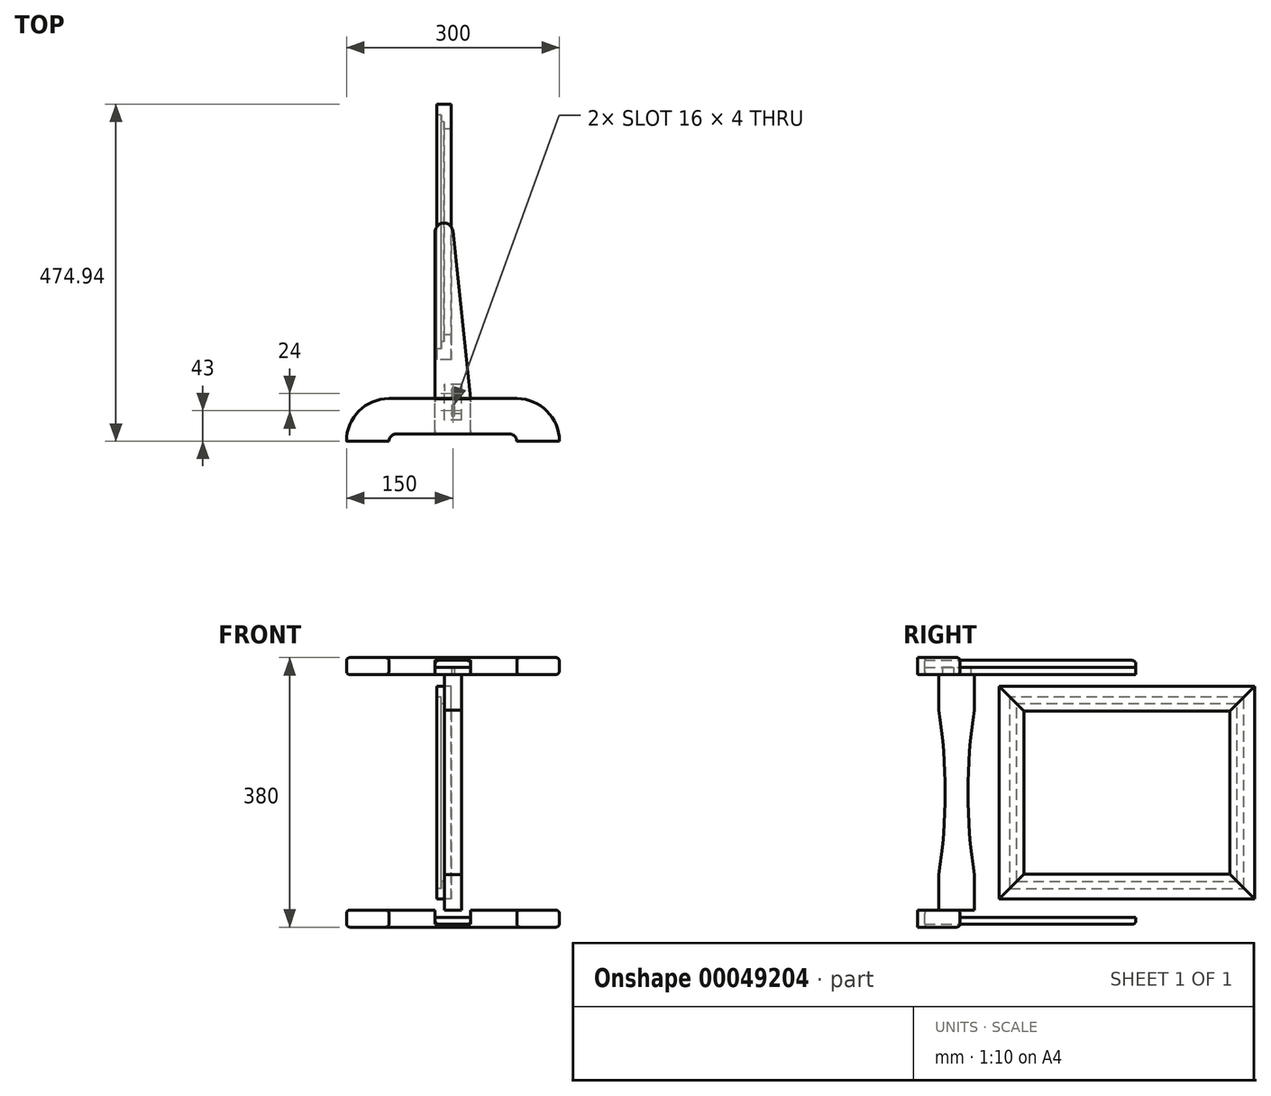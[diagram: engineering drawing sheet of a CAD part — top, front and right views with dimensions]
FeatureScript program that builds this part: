
annotation { "Feature Type Name" : "Feature", "Feature Type Description" : "" }
export const myFeature = defineFeature(function(context is Context, id is Id, definition is map)
    precondition{}
    {
        {
            var Q0;
            Q0=qCreatedBy(makeId("Top.planeOp"),FACE);
            var sketch = newSketch(context, id + "F0", { "sketchPlane" : qUnion([Q0])});
            skLineSegment(sketch, "E0.bottom", {"start": v(150, -30) * mm, "end": v(90, -30) * mm});
            skLineSegment(sketch, "E0.top", {"start": v(90, 30) * mm, "end": v(-90, 30) * mm});
            skPoint(sketch, "E0.middle", {"position": v(0, 0) * mm});
            skArc(sketch, "E1", {"start": v(90, -30) * mm, "mid": v(87.07, -22.93) * mm, "end": v(80, -20) * mm});
            skArc(sketch, "E2", {"start": v(-80, -20) * mm, "mid": v(-87.07, -22.93) * mm, "end": v(-90, -30) * mm});
            skLineSegment(sketch, "E3", {"start": v(-80, -20) * mm, "end": v(80, -20) * mm});
            skArc(sketch, "E4", {"start": v(150, -30) * mm, "mid": v(132.43, 12.43) * mm, "end": v(90, 30) * mm});
            skPoint(sketch, "E0.right.end.orphan", {"position": v(-150, 30) * mm});
            skArc(sketch, "E5.trimOffspring", {"start": v(-90, 30) * mm, "mid": v(-132.43, 12.43) * mm, "end": v(-150, -30) * mm});
            skPoint(sketch, "E0.left.end.orphan", {"position": v(150, 30) * mm});
            skLineSegment(sketch, "E6.trimOffspring", {"start": v(-90, -30) * mm, "end": v(-150, -30) * mm});
            skSolve(sketch);
        }
        {
            var Q0;
            Q0=makeQuery(id+"F0.imprint","IMPRINT",FACE,{"disambiguationData":[TD([[makeQuery(id+"F0.imprint","IMPRINT",EDGE,{"derivedFrom":sQuery(id+"F0.wireOp",EDGE,"E0.bottom")}),-1.0]])]});
            extrude(context, id + "F1", {"entities" : qUnion([Q0]), "depth" : 24 * mm, "offsetDistance" : 25 * mm});
        }
        {
            var Q0;
            Q0=makeQuery(id+"F1.opExtrude","SWEPT_FACE",FACE,{"disambiguationData":[OSD([sQuery(id+"F0.wireOp",EDGE,"E0.top")])]});
            var sketch = newSketch(context, id + "F2", { "sketchPlane" : qUnion([Q0])});
            skLineSegment(sketch, "E7.top", {"start": v(-25, 10) * mm, "end": v(25, 10) * mm});
            skPoint(sketch, "E7.middle", {"position": v(0, 0) * mm});
            skLineSegment(sketch, "E8", {"start": v(25, 0) * mm, "end": v(25, 10) * mm});
            skLineSegment(sketch, "E9", {"start": v(-25, 0) * mm, "end": v(-25, 10) * mm});
            skLineSegment(sketch, "E10", {"start": v(25, 0) * mm, "end": v(-25, 0) * mm});
            skSolve(sketch);
        }
        {
            var Q0;
            Q0=makeQuery(id+"F2.imprint","IMPRINT",FACE,{"disambiguationData":[TD([[makeQuery(id+"F2.imprint","IMPRINT",EDGE,{"derivedFrom":sQuery(id+"F2.wireOp",EDGE,"E7.top")}),-1.0]])]});
            extrude(context, id + "F3", {"entities" : qUnion([Q0]), "operationType" : NewBodyOperationType.REMOVE, "endBound" : BoundingType.THROUGH_ALL, "oppositeDirection" : true, "depth" : 25 * mm, "offsetDistance" : 25 * mm});
        }
        {
            var Q0;
            Q0=makeQuery(id+"F1.opExtrude","CAP_EDGE",EDGE,{"disambiguationData":[OSD([sQuery(id+"F0.wireOp",EDGE,"E5.trimOffspring")])],"isStart":false});
            var Q1;
            Q1=makeQuery(id+"F1.opExtrude","CAP_EDGE",EDGE,{"disambiguationData":[OSD([sQuery(id+"F0.wireOp",EDGE,"E2")])],"isStart":false});
            var Q2;
            Q2=makeQuery(id+"F1.opExtrude","CAP_EDGE",EDGE,{"disambiguationData":[OSD([sQuery(id+"F0.wireOp",EDGE,"E5.trimOffspring")])],"isStart":true});
            var Q3;
            {var subQ0=sQuery(id+"F0.wireOp",EDGE,"E4");var subQ1=sQuery(id+"F0.wireOp",EDGE,"E0.top");Q3=makeQuery(id+"F3.boolean.opBoolean","SPLIT",EDGE,{"disambiguationData":[TD([makeQuery(id+"F1.opExtrude","SWEPT_FACE",FACE,{"disambiguationData":[OSD([subQ0])]})])],"derivedFrom":makeQuery(id+"F1.opExtrude","CAP_EDGE",EDGE,{"disambiguationData":[OSD([subQ1])],"isStart":true})});}
            var Q4;
            Q4=makeQuery(id+"F1.opExtrude","CAP_EDGE",EDGE,{"disambiguationData":[OSD([sQuery(id+"F0.wireOp",EDGE,"E1")])],"isStart":true});
            var Q5;
            {var subQ0=sQuery(id+"F0.wireOp",EDGE,"E3");var subQ1=sQuery(id+"F0.wireOp",EDGE,"E2");Q5=makeQuery(id+"F3.boolean.opBoolean","SPLIT",EDGE,{"disambiguationData":[TD([makeQuery(id+"F1.opExtrude","SWEPT_FACE",FACE,{"disambiguationData":[OSD([subQ1])]})])],"derivedFrom":makeQuery(id+"F1.opExtrude","CAP_EDGE",EDGE,{"disambiguationData":[OSD([subQ0])],"isStart":true})});}
            fillet(context, id + "F4", {"entities" : qUnion([Q0, Q1, Q2, Q3, Q4, Q5]), "radius" : 5 * mm, "tangentPropagation" : true, "allowEdgeOverflow" : false});
        }
        {
            var Q0;
            Q0=qCreatedBy(makeId("Right.planeOp"),FACE);
            var sketch = newSketch(context, id + "F5", { "sketchPlane" : qUnion([Q0])});
            skLineSegment(sketch, "E11", {"start": v(-20.06, 0) * mm, "end": v(29.94, 0) * mm});
            skLineSegment(sketch, "E12", {"start": v(29.94, 0) * mm, "end": v(29.94, -50) * mm});
            skLineSegment(sketch, "E13", {"start": v(29.94, -332) * mm, "end": v(-20.06, -332) * mm});
            skLineSegment(sketch, "E14", {"start": v(-20.06, -332) * mm, "end": v(-20.06, -282) * mm});
            skLineSegment(sketch, "E15", {"start": v(46, -50) * mm, "end": v(-37.65, -50) * mm, "construction": true});
            skLineSegment(sketch, "E16", {"start": v(48.69, -282) * mm, "end": v(-41.5, -282) * mm, "construction": true});
            skArc(sketch, "E17", {"start": v(29.94, -50) * mm, "mid": v(20.92, -166) * mm, "end": v(29.94, -282) * mm});
            skPoint(sketch, "E17.first.point", {"position": v(29.94, -50) * mm});
            skPoint(sketch, "E17.second.point", {"position": v(29.94, -282) * mm});
            skArc(sketch, "E18", {"start": v(-20.06, -282) * mm, "mid": v(-11.03, -166) * mm, "end": v(-20.06, -50) * mm});
            skPoint(sketch, "E18.first.point", {"position": v(-20.06, -50) * mm});
            skPoint(sketch, "E18.second.point", {"position": v(-20.06, -282) * mm});
            skLineSegment(sketch, "E19.trimOffspring", {"start": v(29.94, -282) * mm, "end": v(29.94, -332) * mm});
            skLineSegment(sketch, "E20.trimOffspring", {"start": v(-20.06, -50) * mm, "end": v(-20.06, 0) * mm});
            skSolve(sketch);
        }
        {
            var Q0;
            Q0=makeQuery(id+"F5.imprint","IMPRINT",FACE,{"disambiguationData":[TD([[makeQuery(id+"F5.imprint","IMPRINT",EDGE,{"derivedFrom":sQuery(id+"F5.wireOp",EDGE,"E11")}),-1.0]])]});
            extrude(context, id + "F6", {"entities" : qUnion([Q0]), "depth" : 24 * mm, "offsetDistance" : 25 * mm, "symmetric" : true});
        }
        {
            var Q0;
            Q0=qCreatedBy(makeId("Right.planeOp"),FACE);
            var sketch = newSketch(context, id + "F7", { "sketchPlane" : qUnion([Q0])});
            skLineSegment(sketch, "E21", {"start": v(-60.62, -166) * mm, "end": v(450.96, -166) * mm, "construction": true});
            skLineSegment(sketch, "E22", {"start": v(264.94, 66.23) * mm, "end": v(264.94, -411.72) * mm, "construction": true});
            skLineSegment(sketch, "E23.bottom", {"start": v(84.94, -316) * mm, "end": v(444.94, -316) * mm});
            skLineSegment(sketch, "E23.top", {"start": v(84.94, -16) * mm, "end": v(444.94, -16) * mm});
            skLineSegment(sketch, "E23.left", {"start": v(84.94, -316) * mm, "end": v(84.94, -16) * mm});
            skLineSegment(sketch, "E23.right", {"start": v(444.94, -316) * mm, "end": v(444.94, -16) * mm});
            skPoint(sketch, "E23.middle", {"position": v(264.94, -166) * mm});
            skSolve(sketch);
        }
        {
            var Q0;
            Q0=makeQuery(id+"F6.opExtrude","SWEPT_BODY",BODY,{"disambiguationData":[OSD([sQuery(id+"F5.wireOp",EDGE,"E11"),sQuery(id+"F5.wireOp",EDGE,"E12"),sQuery(id+"F5.wireOp",EDGE,"E13"),sQuery(id+"F5.wireOp",EDGE,"E14"),sQuery(id+"F5.wireOp",EDGE,"E17"),sQuery(id+"F5.wireOp",EDGE,"E18"),sQuery(id+"F5.wireOp",EDGE,"E19.trimOffspring"),sQuery(id+"F5.wireOp",EDGE,"E20.trimOffspring")])]});
            transform(context, id + "F8", {"entities" : qUnion([Q0]), "transformType" : TransformType.TRANSLATION_3D, "dx" : 0 * mm, "dy" : -100 * mm, "dz" : 0 * mm, "makeCopy" : false});
        }
        {
            var Q0;
            Q0=makeQuery(id+"F6.opExtrude","SWEPT_BODY",BODY,{"disambiguationData":[OSD([sQuery(id+"F5.wireOp",EDGE,"E11"),sQuery(id+"F5.wireOp",EDGE,"E12"),sQuery(id+"F5.wireOp",EDGE,"E13"),sQuery(id+"F5.wireOp",EDGE,"E14"),sQuery(id+"F5.wireOp",EDGE,"E17"),sQuery(id+"F5.wireOp",EDGE,"E18"),sQuery(id+"F5.wireOp",EDGE,"E19.trimOffspring"),sQuery(id+"F5.wireOp",EDGE,"E20.trimOffspring")])]});
            transform(context, id + "F9", {"entities" : qUnion([Q0]), "transformType" : TransformType.TRANSLATION_3D, "dx" : 0 * mm, "dy" : 120 * mm, "dz" : 0 * mm, "makeCopy" : false});
        }
        {
            var Q0;
            Q0=makeQuery(id+"F7.imprint","IMPRINT",FACE,{"disambiguationData":[TD([[makeQuery(id+"F7.imprint","IMPRINT",EDGE,{"derivedFrom":sQuery(id+"F7.wireOp",EDGE,"E23.bottom")}),1.0]])]});
            var sketch = newSketch(context, id + "F10", { "sketchPlane" : qUnion([Q0])});
            skLineSegment(sketch, "E24", {"start": v(409.94, -51) * mm, "end": v(409.94, -281) * mm});
            skLineSegment(sketch, "E25", {"start": v(119.94, -51) * mm, "end": v(119.94, -281) * mm});
            skLineSegment(sketch, "E26", {"start": v(409.94, -281) * mm, "end": v(119.94, -281) * mm});
            skLineSegment(sketch, "E27", {"start": v(409.94, -51) * mm, "end": v(119.94, -51) * mm});
            skPoint(sketch, "E28.orphan", {"position": v(69.8, -281) * mm});
            skPoint(sketch, "E29.orphan", {"position": v(69.8, -51) * mm});
            skLineSegment(sketch, "E30", {"start": v(444.94, -16) * mm, "end": v(409.94, -51) * mm});
            skLineSegment(sketch, "E31", {"start": v(119.94, -281) * mm, "end": v(84.94, -316) * mm});
            skLineSegment(sketch, "E32", {"start": v(409.94, -281) * mm, "end": v(444.94, -316) * mm});
            skLineSegment(sketch, "E33", {"start": v(119.94, -51) * mm, "end": v(84.94, -16) * mm});
            skSolve(sketch);
        }
        {
            var Q0;
            Q0=makeQuery(id+"F10.imprint","IMPRINT",FACE,{"disambiguationData":[TD([[makeQuery(id+"F10.imprint","IMPRINT",EDGE,{"derivedFrom":sQuery(id+"F10.wireOp",EDGE,"E24")}),1.0]])]});
            extrude(context, id + "F11", {"entities" : qUnion([Q0]), "depth" : 10 * mm, "offsetDistance" : 25 * mm});
        }
        {
            var Q0;
            Q0=makeQuery(id+"F11.opExtrude","CAP_FACE",FACE,{"disambiguationData":[OSD([sQuery(id+"F7.wireOp",EDGE,"E23.right"),sQuery(id+"F10.wireOp",EDGE,"E24"),sQuery(id+"F10.wireOp",EDGE,"E30"),sQuery(id+"F10.wireOp",EDGE,"E32")])],"isStart":true});
            extrude(context, id + "F12", {"entities" : qUnion([Q0]), "operationType" : NewBodyOperationType.ADD, "depth" : 10 * mm, "offsetDistance" : 25 * mm});
        }
        {
            var Q0;
            Q0=makeQuery(id+"F10.imprint","IMPRINT",FACE,{"disambiguationData":[TD([[makeQuery(id+"F10.imprint","IMPRINT",EDGE,{"derivedFrom":sQuery(id+"F10.wireOp",EDGE,"E25")}),-1.0]])]});
            extrude(context, id + "F13", {"entities" : qUnion([Q0]), "depth" : 10 * mm, "offsetDistance" : 25 * mm});
        }
        {
            var Q0;
            Q0=makeQuery(id+"F13.opExtrude","CAP_FACE",FACE,{"disambiguationData":[OSD([sQuery(id+"F7.wireOp",EDGE,"E23.left"),sQuery(id+"F10.wireOp",EDGE,"E25"),sQuery(id+"F10.wireOp",EDGE,"E31"),sQuery(id+"F10.wireOp",EDGE,"E33")])],"isStart":true});
            extrude(context, id + "F14", {"entities" : qUnion([Q0]), "operationType" : NewBodyOperationType.ADD, "depth" : 10 * mm, "offsetDistance" : 25 * mm});
        }
        {
            var Q0;
            Q0=makeQuery(id+"F10.imprint","IMPRINT",FACE,{"disambiguationData":[TD([[makeQuery(id+"F10.imprint","IMPRINT",EDGE,{"derivedFrom":sQuery(id+"F10.wireOp",EDGE,"E27")}),-1.0]])]});
            extrude(context, id + "F15", {"entities" : qUnion([Q0]), "depth" : 10 * mm, "offsetDistance" : 25 * mm});
        }
        {
            var Q0;
            Q0=makeQuery(id+"F15.opExtrude","CAP_FACE",FACE,{"disambiguationData":[OSD([sQuery(id+"F7.wireOp",EDGE,"E23.top"),sQuery(id+"F10.wireOp",EDGE,"E27"),sQuery(id+"F10.wireOp",EDGE,"E30"),sQuery(id+"F10.wireOp",EDGE,"E33")])],"isStart":true});
            extrude(context, id + "F16", {"entities" : qUnion([Q0]), "depth" : 10 * mm, "offsetDistance" : 25 * mm});
        }
        {
            var Q0;
            Q0=makeQuery(id+"F10.imprint","IMPRINT",FACE,{"disambiguationData":[TD([[makeQuery(id+"F10.imprint","IMPRINT",EDGE,{"derivedFrom":sQuery(id+"F10.wireOp",EDGE,"E26")}),1.0]])]});
            extrude(context, id + "F17", {"entities" : qUnion([Q0]), "depth" : 10 * mm, "offsetDistance" : 25 * mm});
        }
        {
            var Q0;
            Q0=makeQuery(id+"F17.opExtrude","CAP_FACE",FACE,{"disambiguationData":[OSD([sQuery(id+"F7.wireOp",EDGE,"E23.bottom"),sQuery(id+"F10.wireOp",EDGE,"E26"),sQuery(id+"F10.wireOp",EDGE,"E31"),sQuery(id+"F10.wireOp",EDGE,"E32")])],"isStart":true});
            extrude(context, id + "F18", {"entities" : qUnion([Q0]), "depth" : 10 * mm, "offsetDistance" : 25 * mm});
        }
        {
            var Q0;
            Q0=makeQuery(id+"F16.opExtrude","SWEPT_BODY",BODY,{"disambiguationData":[OSD([sQuery(id+"F7.wireOp",EDGE,"E23.top"),sQuery(id+"F10.wireOp",EDGE,"E27"),sQuery(id+"F10.wireOp",EDGE,"E30"),sQuery(id+"F10.wireOp",EDGE,"E33")])]});
            var Q1;
            Q1=makeQuery(id+"F15.opExtrude","SWEPT_BODY",BODY,{"disambiguationData":[OSD([sQuery(id+"F7.wireOp",EDGE,"E23.top"),sQuery(id+"F10.wireOp",EDGE,"E27"),sQuery(id+"F10.wireOp",EDGE,"E30"),sQuery(id+"F10.wireOp",EDGE,"E33")])]});
            booleanBodies(context, id + "F19", {"operationType" : BooleanOperationType.UNION, "tools" : qUnion([Q0, Q1])});
        }
        {
            var Q0;
            Q0=makeQuery(id+"F17.opExtrude","SWEPT_BODY",BODY,{"disambiguationData":[OSD([sQuery(id+"F7.wireOp",EDGE,"E23.bottom"),sQuery(id+"F10.wireOp",EDGE,"E26"),sQuery(id+"F10.wireOp",EDGE,"E31"),sQuery(id+"F10.wireOp",EDGE,"E32")])]});
            var Q1;
            Q1=makeQuery(id+"F18.opExtrude","SWEPT_BODY",BODY,{"disambiguationData":[OSD([sQuery(id+"F7.wireOp",EDGE,"E23.bottom"),sQuery(id+"F10.wireOp",EDGE,"E26"),sQuery(id+"F10.wireOp",EDGE,"E31"),sQuery(id+"F10.wireOp",EDGE,"E32")])]});
            booleanBodies(context, id + "F20", {"operationType" : BooleanOperationType.UNION, "tools" : qUnion([Q0, Q1])});
        }
        {
            var Q0;
            Q0=makeQuery(id+"F12.opExtrude","CAP_FACE",FACE,{"disambiguationData":[OSD([sQuery(id+"F7.wireOp",EDGE,"E23.right"),sQuery(id+"F10.wireOp",EDGE,"E24"),sQuery(id+"F10.wireOp",EDGE,"E30"),sQuery(id+"F10.wireOp",EDGE,"E32")])],"isStart":false});
            var sketch = newSketch(context, id + "F21", { "sketchPlane" : qUnion([Q0])});
            skLineSegment(sketch, "E34", {"start": v(-419.94, -291) * mm, "end": v(-419.94, -41) * mm});
            skSolve(sketch);
        }
        {
            var Q0;
            {var subQ0=sQuery(id+"F21.wireOp",EDGE,"E34");Q0=makeQuery(id+"F21.imprint","IMPRINT",FACE,{"disambiguationData":[TD([[makeQuery(id+"F21.imprint","IMPRINT",EDGE,{"derivedFrom":subQ0}),-1.0]])]});}
            extrude(context, id + "F22", {"entities" : qUnion([Q0]), "operationType" : NewBodyOperationType.REMOVE, "oppositeDirection" : true, "depth" : 10 * mm, "offsetDistance" : 25 * mm});
        }
        {
            var Q0;
            Q0=makeQuery(id+"F12.opExtrude","CAP_FACE",FACE,{"disambiguationData":[OSD([sQuery(id+"F7.wireOp",EDGE,"E23.right"),sQuery(id+"F10.wireOp",EDGE,"E24"),sQuery(id+"F10.wireOp",EDGE,"E30"),sQuery(id+"F10.wireOp",EDGE,"E32")])],"isStart":false});
            var sketch = newSketch(context, id + "F23", { "sketchPlane" : qUnion([Q0])});
            skLineSegment(sketch, "E35", {"start": v(-429.94, -301) * mm, "end": v(-429.94, -31) * mm});
            skSolve(sketch);
        }
        {
            var Q0;
            Q0 = qSketchRegion(id + "F23", true);
            var Q1;
            {var subQ0=sQuery(id+"F23.wireOp",EDGE,"E35");Q1=makeQuery(id+"F23.imprint","IMPRINT",FACE,{"disambiguationData":[TD([[makeQuery(id+"F23.imprint","IMPRINT",EDGE,{"derivedFrom":subQ0}),-1.0]])]});}
            extrude(context, id + "F24", {"entities" : qUnion([Q0, Q1]), "operationType" : NewBodyOperationType.REMOVE, "oppositeDirection" : true, "depth" : 6 * mm, "offsetDistance" : 25 * mm});
        }
        {
            var Q0;
            Q0=makeQuery(id+"F16.opExtrude","CAP_FACE",FACE,{"disambiguationData":[OSD([sQuery(id+"F7.wireOp",EDGE,"E23.top"),sQuery(id+"F10.wireOp",EDGE,"E27"),sQuery(id+"F10.wireOp",EDGE,"E30"),sQuery(id+"F10.wireOp",EDGE,"E33")])],"isStart":false});
            var sketch = newSketch(context, id + "F25", { "sketchPlane" : qUnion([Q0])});
            skLineSegment(sketch, "E36", {"start": v(-419.94, -41) * mm, "end": v(-109.94, -41) * mm});
            skSolve(sketch);
        }
        {
            var Q0;
            Q0 = qSketchRegion(id + "F25", true);
            var Q1;
            {var subQ0=sQuery(id+"F25.wireOp",EDGE,"E36");Q1=makeQuery(id+"F25.imprint","IMPRINT",FACE,{"disambiguationData":[TD([[makeQuery(id+"F25.imprint","IMPRINT",EDGE,{"derivedFrom":subQ0}),-1.0]])]});}
            extrude(context, id + "F26", {"entities" : qUnion([Q0, Q1]), "operationType" : NewBodyOperationType.REMOVE, "oppositeDirection" : true, "depth" : 10 * mm, "offsetDistance" : 25 * mm});
        }
        {
            var Q0;
            Q0=makeQuery(id+"F16.opExtrude","CAP_FACE",FACE,{"disambiguationData":[OSD([sQuery(id+"F7.wireOp",EDGE,"E23.top"),sQuery(id+"F10.wireOp",EDGE,"E27"),sQuery(id+"F10.wireOp",EDGE,"E30"),sQuery(id+"F10.wireOp",EDGE,"E33")])],"isStart":false});
            var sketch = newSketch(context, id + "F27", { "sketchPlane" : qUnion([Q0])});
            skLineSegment(sketch, "E37", {"start": v(-429.94, -31) * mm, "end": v(-99.94, -31) * mm});
            skSolve(sketch);
        }
        {
            var Q0;
            Q0 = qSketchRegion(id + "F27", true);
            var Q1;
            {var subQ0=sQuery(id+"F27.wireOp",EDGE,"E37");Q1=makeQuery(id+"F27.imprint","IMPRINT",FACE,{"disambiguationData":[TD([[makeQuery(id+"F27.imprint","IMPRINT",EDGE,{"derivedFrom":subQ0}),-1.0]])]});}
            extrude(context, id + "F28", {"entities" : qUnion([Q0, Q1]), "operationType" : NewBodyOperationType.REMOVE, "oppositeDirection" : true, "depth" : 6 * mm, "offsetDistance" : 25 * mm});
        }
        {
            var Q0;
            Q0=makeQuery(id+"F18.opExtrude","CAP_FACE",FACE,{"disambiguationData":[OSD([sQuery(id+"F7.wireOp",EDGE,"E23.bottom"),sQuery(id+"F10.wireOp",EDGE,"E26"),sQuery(id+"F10.wireOp",EDGE,"E31"),sQuery(id+"F10.wireOp",EDGE,"E32")])],"isStart":false});
            var sketch = newSketch(context, id + "F29", { "sketchPlane" : qUnion([Q0])});
            skLineSegment(sketch, "E38", {"start": v(-109.94, -291) * mm, "end": v(-419.94, -291) * mm});
            skSolve(sketch);
        }
        {
            var Q0;
            Q0 = qSketchRegion(id + "F29", true);
            var Q1;
            {var subQ0=sQuery(id+"F29.wireOp",EDGE,"E38");Q1=makeQuery(id+"F29.imprint","IMPRINT",FACE,{"disambiguationData":[TD([[makeQuery(id+"F29.imprint","IMPRINT",EDGE,{"derivedFrom":subQ0}),-1.0]])]});}
            extrude(context, id + "F30", {"entities" : qUnion([Q0, Q1]), "operationType" : NewBodyOperationType.REMOVE, "oppositeDirection" : true, "depth" : 10 * mm, "offsetDistance" : 25 * mm});
        }
        {
            var Q0;
            Q0=makeQuery(id+"F18.opExtrude","CAP_FACE",FACE,{"disambiguationData":[OSD([sQuery(id+"F7.wireOp",EDGE,"E23.bottom"),sQuery(id+"F10.wireOp",EDGE,"E26"),sQuery(id+"F10.wireOp",EDGE,"E31"),sQuery(id+"F10.wireOp",EDGE,"E32")])],"isStart":false});
            var sketch = newSketch(context, id + "F31", { "sketchPlane" : qUnion([Q0])});
            skLineSegment(sketch, "E39", {"start": v(-99.94, -301) * mm, "end": v(-429.94, -301) * mm});
            skSolve(sketch);
        }
        {
            var Q0;
            Q0 = qSketchRegion(id + "F31", true);
            var Q1;
            {var subQ0=sQuery(id+"F31.wireOp",EDGE,"E39");Q1=makeQuery(id+"F31.imprint","IMPRINT",FACE,{"disambiguationData":[TD([[makeQuery(id+"F31.imprint","IMPRINT",EDGE,{"derivedFrom":subQ0}),-1.0]])]});}
            extrude(context, id + "F32", {"entities" : qUnion([Q0, Q1]), "operationType" : NewBodyOperationType.REMOVE, "oppositeDirection" : true, "depth" : 6 * mm, "offsetDistance" : 25 * mm});
        }
        {
            var Q0;
            Q0=makeQuery(id+"F14.opExtrude","CAP_FACE",FACE,{"disambiguationData":[OSD([sQuery(id+"F7.wireOp",EDGE,"E23.left"),sQuery(id+"F10.wireOp",EDGE,"E25"),sQuery(id+"F10.wireOp",EDGE,"E31"),sQuery(id+"F10.wireOp",EDGE,"E33")])],"isStart":false});
            var sketch = newSketch(context, id + "F33", { "sketchPlane" : qUnion([Q0])});
            skLineSegment(sketch, "E40", {"start": v(-109.94, -291) * mm, "end": v(-109.94, -41) * mm});
            skSolve(sketch);
        }
        {
            var Q0;
            Q0 = qSketchRegion(id + "F33", true);
            var Q1;
            {var subQ0=sQuery(id+"F33.wireOp",EDGE,"E40");Q1=makeQuery(id+"F33.imprint","IMPRINT",FACE,{"disambiguationData":[TD([[makeQuery(id+"F33.imprint","IMPRINT",EDGE,{"derivedFrom":subQ0}),1.0]])]});}
            extrude(context, id + "F34", {"entities" : qUnion([Q0, Q1]), "operationType" : NewBodyOperationType.REMOVE, "oppositeDirection" : true, "depth" : 10 * mm, "offsetDistance" : 25 * mm});
        }
        {
            var Q0;
            Q0=makeQuery(id+"F14.opExtrude","CAP_FACE",FACE,{"disambiguationData":[OSD([sQuery(id+"F7.wireOp",EDGE,"E23.left"),sQuery(id+"F10.wireOp",EDGE,"E25"),sQuery(id+"F10.wireOp",EDGE,"E31"),sQuery(id+"F10.wireOp",EDGE,"E33")])],"isStart":false});
            var sketch = newSketch(context, id + "F35", { "sketchPlane" : qUnion([Q0])});
            skLineSegment(sketch, "E41", {"start": v(-99.94, -301) * mm, "end": v(-99.94, -31) * mm});
            skSolve(sketch);
        }
        {
            var Q0;
            Q0 = qSketchRegion(id + "F35", true);
            var Q1;
            {var subQ0=sQuery(id+"F35.wireOp",EDGE,"E41");Q1=makeQuery(id+"F35.imprint","IMPRINT",FACE,{"disambiguationData":[TD([[makeQuery(id+"F35.imprint","IMPRINT",EDGE,{"derivedFrom":subQ0}),1.0]])]});}
            extrude(context, id + "F36", {"entities" : qUnion([Q0, Q1]), "operationType" : NewBodyOperationType.REMOVE, "oppositeDirection" : true, "depth" : 6 * mm, "offsetDistance" : 25 * mm});
        }
        {
            var Q0;
            Q0=makeQuery(id+"F3.boolean.opBoolean","COPY",FACE,{"derivedFrom":makeQuery(id+"F3.opExtrude","SWEPT_FACE",FACE,{"disambiguationData":[OSD([sQuery(id+"F2.wireOp",EDGE,"E7.top")])]})});
            var sketch = newSketch(context, id + "F37", { "sketchPlane" : qUnion([Q0])});
            skLineSegment(sketch, "E42", {"start": v(25, -30) * mm, "end": v(25, 20) * mm});
            skLineSegment(sketch, "E43", {"start": v(25, 20) * mm, "end": v(-25, 20) * mm});
            skLineSegment(sketch, "E44", {"start": v(-25, 20) * mm, "end": v(-25, -367.5) * mm});
            skLineSegment(sketch, "E45", {"start": v(118.88, -265) * mm, "end": v(-159.6, -265) * mm, "construction": true});
            skLineSegment(sketch, "E46", {"start": v(-12.5, -305.3) * mm, "end": v(-12.5, 20) * mm, "construction": true});
            skArc(sketch, "E47", {"start": v(-25, -265) * mm, "mid": v(-12.5, -277.5) * mm, "end": v(0, -265) * mm});
            skLineSegment(sketch, "E48", {"start": v(25, -30) * mm, "end": v(-0.07, -266.32) * mm});
            skSolve(sketch);
        }
        {
            var Q0;
            Q0=makeQuery(id+"F37.imprint","IMPRINT",FACE,{"disambiguationData":[TD([[makeQuery(id+"F37.imprint","IMPRINT",EDGE,{"derivedFrom":sQuery(id+"F37.wireOp",EDGE,"E42")}),-1.0]])]});
            var Q1;
            {var subQ4=sQuery(id+"F37.wireOp",EDGE,"E48");Q1=makeQuery(id+"F37.imprint","IMPRINT",FACE,{"disambiguationData":[TD([[makeQuery(id+"F37.imprint","IMPRINT",EDGE,{"derivedFrom":subQ4}),-1.0]])]});}
            extrude(context, id + "F38", {"entities" : qUnion([Q0, Q1]), "depth" : 10 * mm, "offsetDistance" : 25 * mm});
        }
        {
            var Q0;
            Q0=makeQuery(id+"F38.opExtrude","CAP_FACE",FACE,{"disambiguationData":[OSD([sQuery(id+"F37.wireOp",EDGE,"E42"),sQuery(id+"F37.wireOp",EDGE,"E43"),sQuery(id+"F37.wireOp",EDGE,"E44"),sQuery(id+"F37.wireOp",EDGE,"E47"),sQuery(id+"F37.wireOp",EDGE,"E48")])],"isStart":true});
            extrude(context, id + "F39", {"entities" : qUnion([Q0]), "depth" : 10 * mm, "offsetDistance" : 25 * mm});
        }
        {
            var Q0;
            Q0=makeQuery(id+"F39.opExtrude","CAP_FACE",FACE,{"disambiguationData":[OSD([sQuery(id+"F37.wireOp",EDGE,"E42"),sQuery(id+"F37.wireOp",EDGE,"E43"),sQuery(id+"F37.wireOp",EDGE,"E44"),sQuery(id+"F37.wireOp",EDGE,"E47"),sQuery(id+"F37.wireOp",EDGE,"E48")])],"isStart":false});
            var sketch = newSketch(context, id + "F40", { "sketchPlane" : qUnion([Q0])});
            skLineSegment(sketch, "E49", {"start": v(25, 30) * mm, "end": v(-25, 30) * mm});
            skSolve(sketch);
        }
        {
            var Q0;
            Q0 = qSketchRegion(id + "F40", true);
            var Q1;
            {var subQ0=sQuery(id+"F40.wireOp",EDGE,"E49");Q1=makeQuery(id+"F40.imprint","IMPRINT",FACE,{"disambiguationData":[TD([[makeQuery(id+"F40.imprint","IMPRINT",EDGE,{"derivedFrom":subQ0}),1.0]])]});}
            extrude(context, id + "F41", {"entities" : qUnion([Q0, Q1]), "operationType" : NewBodyOperationType.REMOVE, "oppositeDirection" : true, "depth" : 10 * mm, "offsetDistance" : 25 * mm});
        }
        {
            var Q0;
            Q0=makeQuery(id+"F39.opExtrude","CAP_EDGE",EDGE,{"disambiguationData":[OSD([sQuery(id+"F37.wireOp",EDGE,"E48")])],"isStart":false});
            fillet(context, id + "F42", {"entities" : qUnion([Q0]), "tangentPropagation" : true, "radius" : 5 * mm, "defaultsChanged" : false, "vertexSettings" : [], "allowEdgeOverflow" : false});
        }
        {
            var Q0;
            Q0=makeQuery(id+"F1.opExtrude","SWEPT_BODY",BODY,{"disambiguationData":[OSD([sQuery(id+"F0.wireOp",EDGE,"E0.bottom"),sQuery(id+"F0.wireOp",EDGE,"E0.top"),sQuery(id+"F0.wireOp",EDGE,"E1"),sQuery(id+"F0.wireOp",EDGE,"E2"),sQuery(id+"F0.wireOp",EDGE,"E3"),sQuery(id+"F0.wireOp",EDGE,"E4"),sQuery(id+"F0.wireOp",EDGE,"E5.trimOffspring"),sQuery(id+"F0.wireOp",EDGE,"E6.trimOffspring")])]});
            var Q1;
            Q1=makeQuery(id+"F39.opExtrude","SWEPT_BODY",BODY,{"disambiguationData":[OSD([sQuery(id+"F37.wireOp",EDGE,"E42"),sQuery(id+"F37.wireOp",EDGE,"E43"),sQuery(id+"F37.wireOp",EDGE,"E44"),sQuery(id+"F37.wireOp",EDGE,"E47"),sQuery(id+"F37.wireOp",EDGE,"E48")])]});
            var Q2;
            Q2=makeQuery(id+"F38.opExtrude","CAP_FACE",FACE,{"disambiguationData":[OSD([sQuery(id+"F37.wireOp",EDGE,"E42"),sQuery(id+"F37.wireOp",EDGE,"E43"),sQuery(id+"F37.wireOp",EDGE,"E44"),sQuery(id+"F37.wireOp",EDGE,"E47"),sQuery(id+"F37.wireOp",EDGE,"E48")])],"isStart":false});
            mirror(context, id + "F43", {"entities" : qUnion([Q0, Q1]), "mirrorPlane" : qUnion([Q2])});
        }
        {
            var Q0;
            Q0=makeQuery(id+"F43.opPattern","COPY",BODY,{"derivedFrom":makeQuery(id+"F1.opExtrude","SWEPT_BODY",BODY,{"disambiguationData":[OSD([sQuery(id+"F0.wireOp",EDGE,"E0.bottom"),sQuery(id+"F0.wireOp",EDGE,"E0.top"),sQuery(id+"F0.wireOp",EDGE,"E1"),sQuery(id+"F0.wireOp",EDGE,"E2"),sQuery(id+"F0.wireOp",EDGE,"E3"),sQuery(id+"F0.wireOp",EDGE,"E4"),sQuery(id+"F0.wireOp",EDGE,"E5.trimOffspring"),sQuery(id+"F0.wireOp",EDGE,"E6.trimOffspring")])]}),"instanceName":"1"});
            var Q1;
            Q1=makeQuery(id+"F43.opPattern","COPY",BODY,{"derivedFrom":makeQuery(id+"F39.opExtrude","SWEPT_BODY",BODY,{"disambiguationData":[OSD([sQuery(id+"F37.wireOp",EDGE,"E42"),sQuery(id+"F37.wireOp",EDGE,"E43"),sQuery(id+"F37.wireOp",EDGE,"E44"),sQuery(id+"F37.wireOp",EDGE,"E47"),sQuery(id+"F37.wireOp",EDGE,"E48")])]}),"instanceName":"1"});
            transform(context, id + "F44", {"entities" : qUnion([Q0, Q1]), "transformType" : TransformType.TRANSLATION_3D, "dx" : 0 * mm, "dy" : 0 * mm, "dz" : -332 * mm, "makeCopy" : false});
        }
        {
            var Q0;
            Q0=makeQuery(id+"F11.opExtrude","SWEPT_BODY",BODY,{"disambiguationData":[OSD([sQuery(id+"F7.wireOp",EDGE,"E23.right"),sQuery(id+"F10.wireOp",EDGE,"E24"),sQuery(id+"F10.wireOp",EDGE,"E30"),sQuery(id+"F10.wireOp",EDGE,"E32")])]});
            var Q1;
            Q1=makeQuery(id+"F17.opExtrude","SWEPT_BODY",BODY,{"disambiguationData":[OSD([sQuery(id+"F7.wireOp",EDGE,"E23.bottom"),sQuery(id+"F10.wireOp",EDGE,"E26"),sQuery(id+"F10.wireOp",EDGE,"E31"),sQuery(id+"F10.wireOp",EDGE,"E32")])]});
            var Q2;
            Q2=makeQuery(id+"F16.opExtrude","SWEPT_BODY",BODY,{"disambiguationData":[OSD([sQuery(id+"F7.wireOp",EDGE,"E23.top"),sQuery(id+"F10.wireOp",EDGE,"E27"),sQuery(id+"F10.wireOp",EDGE,"E30"),sQuery(id+"F10.wireOp",EDGE,"E33")])]});
            var Q3;
            Q3=makeQuery(id+"F13.opExtrude","SWEPT_BODY",BODY,{"disambiguationData":[OSD([sQuery(id+"F7.wireOp",EDGE,"E23.left"),sQuery(id+"F10.wireOp",EDGE,"E25"),sQuery(id+"F10.wireOp",EDGE,"E31"),sQuery(id+"F10.wireOp",EDGE,"E33")])]});
            transform(context, id + "F45", {"entities" : qUnion([Q0, Q1, Q2, Q3]), "transformType" : TransformType.TRANSLATION_3D, "dx" : 0 * mm, "dy" : 0 * mm, "dz" : -0.5 * mm, "makeCopy" : false});
        }
        {
            var Q0;
            Q0=makeQuery(id+"F11.opExtrude","SWEPT_BODY",BODY,{"disambiguationData":[OSD([sQuery(id+"F7.wireOp",EDGE,"E23.right"),sQuery(id+"F10.wireOp",EDGE,"E24"),sQuery(id+"F10.wireOp",EDGE,"E30"),sQuery(id+"F10.wireOp",EDGE,"E32")])]});
            var Q1;
            Q1=makeQuery(id+"F17.opExtrude","SWEPT_BODY",BODY,{"disambiguationData":[OSD([sQuery(id+"F7.wireOp",EDGE,"E23.bottom"),sQuery(id+"F10.wireOp",EDGE,"E26"),sQuery(id+"F10.wireOp",EDGE,"E31"),sQuery(id+"F10.wireOp",EDGE,"E32")])]});
            var Q2;
            Q2=makeQuery(id+"F16.opExtrude","SWEPT_BODY",BODY,{"disambiguationData":[OSD([sQuery(id+"F7.wireOp",EDGE,"E23.top"),sQuery(id+"F10.wireOp",EDGE,"E27"),sQuery(id+"F10.wireOp",EDGE,"E30"),sQuery(id+"F10.wireOp",EDGE,"E33")])]});
            var Q3;
            Q3=makeQuery(id+"F13.opExtrude","SWEPT_BODY",BODY,{"disambiguationData":[OSD([sQuery(id+"F7.wireOp",EDGE,"E23.left"),sQuery(id+"F10.wireOp",EDGE,"E25"),sQuery(id+"F10.wireOp",EDGE,"E31"),sQuery(id+"F10.wireOp",EDGE,"E33")])]});
            transform(context, id + "F46", {"entities" : qUnion([Q0, Q1, Q2, Q3]), "transformType" : TransformType.TRANSLATION_3D, "dx" : -12.5 * mm, "dy" : 0 * mm, "dz" : 0 * mm, "makeCopy" : false});
        }
        {
            var Q0;
            Q0=makeQuery(id+"F38.opExtrude","CAP_FACE",FACE,{"disambiguationData":[OSD([sQuery(id+"F37.wireOp",EDGE,"E42"),sQuery(id+"F37.wireOp",EDGE,"E43"),sQuery(id+"F37.wireOp",EDGE,"E44"),sQuery(id+"F37.wireOp",EDGE,"E47"),sQuery(id+"F37.wireOp",EDGE,"E48")])],"isStart":false});
            var sketch = newSketch(context, id + "F47", { "sketchPlane" : qUnion([Q0])});
            skLineSegment(sketch, "E50", {"start": v(0, 20) * mm, "end": v(0, -94.47) * mm, "construction": true});
            skLineSegment(sketch, "E51", {"start": v(12.9, -7) * mm, "end": v(-12.76, -7) * mm, "construction": true});
            skLineSegment(sketch, "E52", {"start": v(12.9, -19) * mm, "end": v(-13.26, -19) * mm, "construction": true});
            skLineSegment(sketch, "E53", {"start": v(13.15, -31) * mm, "end": v(-13.01, -31) * mm, "construction": true});
            skLineSegment(sketch, "E54", {"start": v(14.16, -43) * mm, "end": v(-12.76, -43) * mm, "construction": true});
            skArc(sketch, "E55", {"start": v(-2, -43) * mm, "mid": v(0, -45) * mm, "end": v(2, -43) * mm});
            skArc(sketch, "E56", {"start": v(2, -31) * mm, "mid": v(0, -29) * mm, "end": v(-2, -31) * mm});
            skArc(sketch, "E57", {"start": v(-2, -19) * mm, "mid": v(0, -21) * mm, "end": v(2, -19) * mm});
            skArc(sketch, "E58", {"start": v(2, -7) * mm, "mid": v(0, -5) * mm, "end": v(-2, -7) * mm});
            skLineSegment(sketch, "E59", {"start": v(2, -43) * mm, "end": v(2, -31) * mm});
            skLineSegment(sketch, "E60", {"start": v(-2, -43) * mm, "end": v(-2, -31) * mm});
            skLineSegment(sketch, "E61", {"start": v(2, -19) * mm, "end": v(2, -7) * mm});
            skLineSegment(sketch, "E62", {"start": v(-2, -19) * mm, "end": v(-2, -7) * mm});
            skSolve(sketch);
        }
        {
            var Q0;
            Q0=makeQuery(id+"F47.imprint","IMPRINT",FACE,{"disambiguationData":[TD([[makeQuery(id+"F47.imprint","IMPRINT",EDGE,{"derivedFrom":sQuery(id+"F47.wireOp",EDGE,"E57")}),1.0]])]});
            var Q1;
            Q1=makeQuery(id+"F47.imprint","IMPRINT",FACE,{"disambiguationData":[TD([[makeQuery(id+"F47.imprint","IMPRINT",EDGE,{"derivedFrom":sQuery(id+"F47.wireOp",EDGE,"E55")}),1.0]])]});
            extrude(context, id + "F48", {"entities" : qUnion([Q0, Q1]), "operationType" : NewBodyOperationType.REMOVE, "oppositeDirection" : true, "depth" : 10 * mm, "offsetDistance" : 25 * mm});
        }
    });
